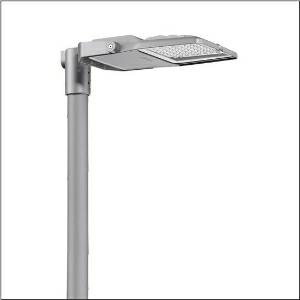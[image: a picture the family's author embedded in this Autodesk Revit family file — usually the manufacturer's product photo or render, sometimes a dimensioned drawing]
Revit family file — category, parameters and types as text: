
# Revit family: floodlight_fl_21_iq_mini___pl61_5xa7771d2c3a_41a8
name_source: partatom
category: Lighting Fixtures
units: mm (PartAtom-declared; Revit-internal decimal feet)

## family parameters
Cut with Voids When Loaded = No
Host = Face
Light Source = No
Part Type = Normal
Room Calculation Point = No
Round Connector Dimension = Use Diameter
Shared = No

## types (1)
- --- (1 x LED, 17500 lm, 143 W, 3000K)
    Apparent Load = 143 VA
    CIE Flux Codes = 33 65 98 100 100
    Color Rendering = 70
    Color Temperature = 3000K
    Default Elevation = 1800 mm
    Description = Floodlight FL 21 iQ mini, floodlight, primary light control with lens, of PMMA, primary optical cover: protective disc, of toughened safety glass, transparent, light distribution: PL61, light emission: direct distribution, installation type: surface-mounted, LED, High Power LED, rated luminous flux: 17.500lm, luminous efficacy: 122lm/W, light colour: 730, colour temperature: 3000K, control gear: iQ Comfort/DALI, control: Auto-Match, Temp-Guard, Lumen-Switch, Night-Set, Smart-Wire, Light-Fading, Desk-Remote (wireless, voltage-free reading and setting of iQ features in the workshop via application-optimized NFC function/RFID function), optimised constant luminous flux control (CLO 2.0), with terminal, 6-pole, mains connection: 220..240V, AC, 50/60Hz, start of lifetime: 143W, end of service life: 152W, reduction: 61W, luminaire housing, of diecast aluminium, powder-coated, Siteco® metallic grey (DB 702S), corrosivity category C5 mid according to DIN EN ISO 12944, suitable for swimming pools, chlorine-resistant, sealing non-destructively replaceable, please order mast flange separately, mast bracket, of steel, galvanised, powder-coated, Siteco® metallic grey (DB 702S), protection rating (complete): IP66, insulation class (complete): insulation class II (safety insulation), certification: CE, ENEC, VDE, protection symbol: D, impact resistance: IK08, permissible operating ambient temperature: -40..+40°C, permissible operating ambient temperature for outdoor applications: -40..+50°C, standard: DIN EN 12944, LABS conformity tested according to VDMA 24364:2018-05, packaging unit: 1 piece

Light Distribution: PL61
    Height = 70 mm
    Lamp = 1 x LED
    Lamp Light Flux = 17500 lm
    Lamp Power = 143 W
    Lamp count = 1
    Length = 485 mm
    Luminous efficacy = 122 lm/W
    Manufacturer = Siteco
    ModVariant = No
    Model = 5XA7771D2C3A
    Number of Poles = 1
    OnlyDefault = Yes
    Power Factor = 1
    Product Name = Floodlight FL 21 iQ mini | PL61
    Product group = floodlight | pylon annexe
    ProductGroupID = 6200
    Protection Class = Protection class II
    Protection Degree = IP 66
    RLX_Detail_Level = 1
    RLX_Emergency_Light_Flux = 0 lm
    RLX_Emergency_Type = 0
    RLX_Emergency_Type_DB = No
    RlxData = <blob elided: 101797 chars, md5=4b2e5544>
    Socket = socket
    Standby Power = 0 W
    System Light Flux = 17500 lm
    System Power = 143 W
    Type Comments = factory setting: luminous flux: 100 % | dim-lin: 254 | 730 mA
    Type Image = l_1007125.jpg
    URL = http://relux.com
    VarID = @adj_172718
    Voltage = 0 V
    Weight = 0.00 kg
    Width = 337 mm

## geometry (parser evidence)
native form markers: Blend x4, Sweep x12
no freeform markers — native parametric forms only
